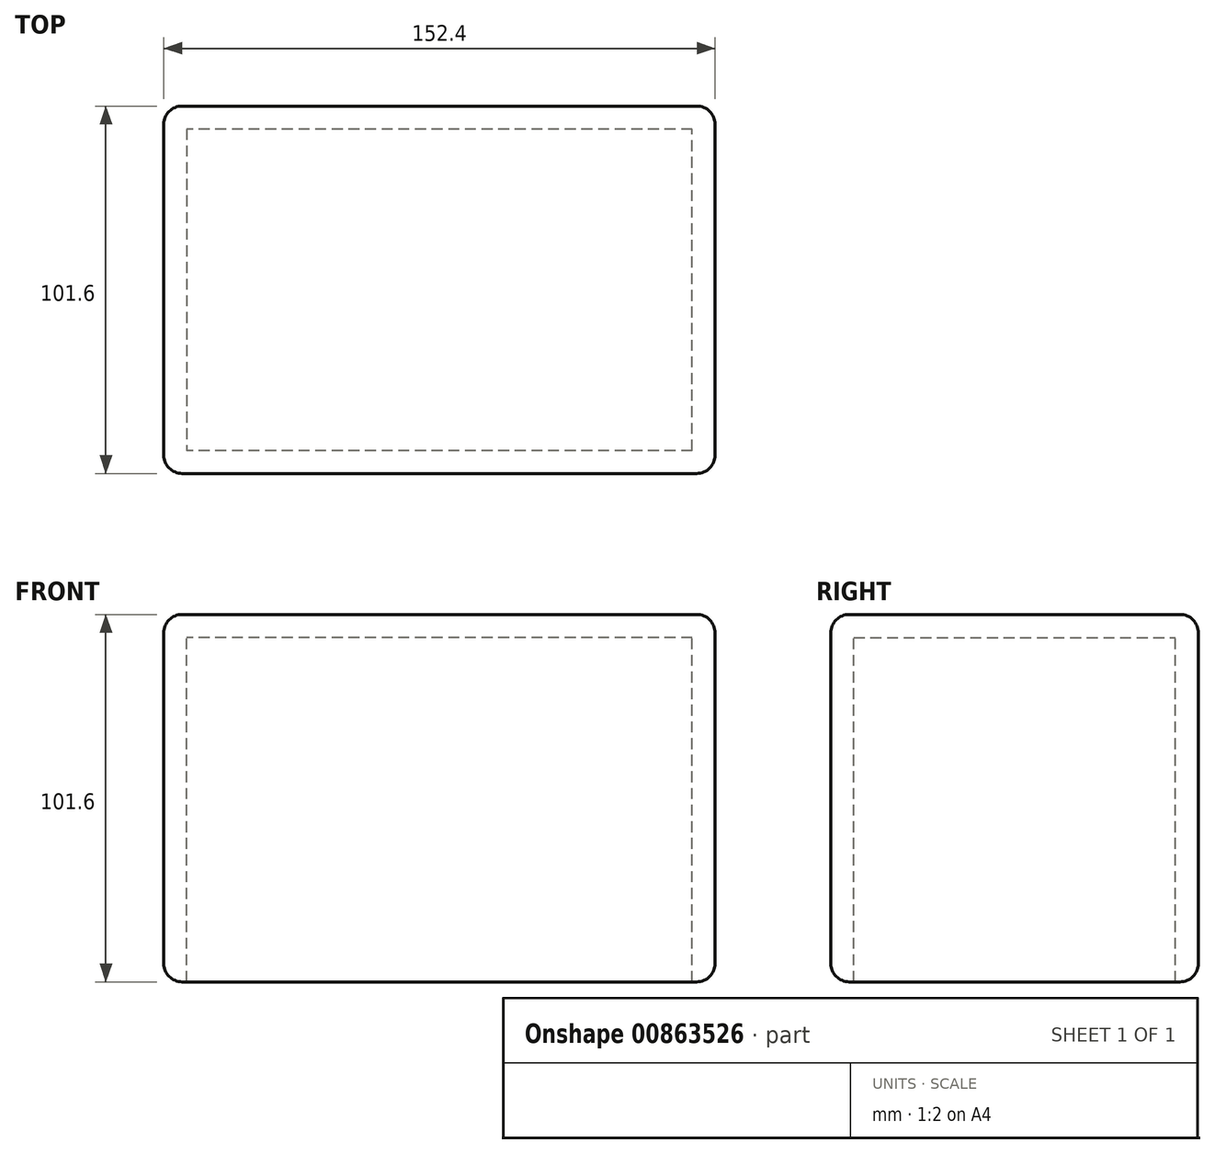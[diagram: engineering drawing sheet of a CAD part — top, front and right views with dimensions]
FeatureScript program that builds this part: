
annotation { "Feature Type Name" : "Feature", "Feature Type Description" : "" }
export const myFeature = defineFeature(function(context is Context, id is Id, definition is map)
    precondition{}
    {
        {
            var Q0;
            Q0=qCreatedBy(makeId("Top.planeOp"),FACE);
            var sketch = newSketch(context, id + "F0", { "sketchPlane" : qUnion([Q0])});
            skLineSegment(sketch, "E0.bottom", {"start": v(-111.11, 101.6) * mm, "end": v(41.29, 101.6) * mm});
            skLineSegment(sketch, "E0.top", {"start": v(-111.11, 0) * mm, "end": v(41.29, 0) * mm});
            skLineSegment(sketch, "E0.left", {"start": v(-111.11, 101.6) * mm, "end": v(-111.11, 0) * mm});
            skLineSegment(sketch, "E0.right", {"start": v(41.29, 101.6) * mm, "end": v(41.29, 0) * mm});
            skSolve(sketch);
        }
        {
            var Q0;
            Q0=makeQuery(id+"F0.imprint","IMPRINT",FACE,{"disambiguationData":[TD([[makeQuery(id+"F0.imprint","IMPRINT",EDGE,{"derivedFrom":sQuery(id+"F0.wireOp",EDGE,"E0.bottom")}),-1.0]])]});
            extrude(context, id + "F1", {"entities" : qUnion([Q0]), "depth" : 101.6 * mm, "offsetDistance" : 25.4 * mm});
        }
        {
            var Q0;
            Q0=makeQuery(id+"F1.opExtrude","CAP_EDGE",EDGE,{"disambiguationData":[OSD([sQuery(id+"F0.wireOp",EDGE,"E0.bottom")])],"isStart":false});
            var Q1;
            Q1=makeQuery(id+"F1.opExtrude","CAP_EDGE",EDGE,{"disambiguationData":[OSD([sQuery(id+"F0.wireOp",EDGE,"E0.left")])],"isStart":false});
            var Q2;
            Q2=makeQuery(id+"F1.opExtrude","CAP_EDGE",EDGE,{"disambiguationData":[OSD([sQuery(id+"F0.wireOp",EDGE,"E0.top")])],"isStart":false});
            var Q3;
            Q3=makeQuery(id+"F1.opExtrude","CAP_EDGE",EDGE,{"disambiguationData":[OSD([sQuery(id+"F0.wireOp",EDGE,"E0.right")])],"isStart":false});
            var Q4;
            Q4=makeQuery(id+"F1.opExtrude","SWEPT_EDGE",EDGE,{"disambiguationData":[OSD([sQuery(id+"F0.wireOp",EDGE,"E0.top"),sQuery(id+"F0.wireOp",EDGE,"E0.right")])]});
            var Q5;
            Q5=makeQuery(id+"F1.opExtrude","SWEPT_EDGE",EDGE,{"disambiguationData":[OSD([sQuery(id+"F0.wireOp",EDGE,"E0.top"),sQuery(id+"F0.wireOp",EDGE,"E0.left")])]});
            var Q6;
            Q6=makeQuery(id+"F1.opExtrude","SWEPT_EDGE",EDGE,{"disambiguationData":[OSD([sQuery(id+"F0.wireOp",EDGE,"E0.bottom"),sQuery(id+"F0.wireOp",EDGE,"E0.left")])]});
            var Q7;
            Q7=makeQuery(id+"F1.opExtrude","SWEPT_EDGE",EDGE,{"disambiguationData":[OSD([sQuery(id+"F0.wireOp",EDGE,"E0.bottom"),sQuery(id+"F0.wireOp",EDGE,"E0.right")])]});
            var Q8;
            Q8=makeQuery(id+"F1.opExtrude","CAP_EDGE",EDGE,{"disambiguationData":[OSD([sQuery(id+"F0.wireOp",EDGE,"E0.top")])],"isStart":true});
            var Q9;
            Q9=makeQuery(id+"F1.opExtrude","CAP_EDGE",EDGE,{"disambiguationData":[OSD([sQuery(id+"F0.wireOp",EDGE,"E0.left")])],"isStart":true});
            var Q10;
            Q10=makeQuery(id+"F1.opExtrude","CAP_EDGE",EDGE,{"disambiguationData":[OSD([sQuery(id+"F0.wireOp",EDGE,"E0.bottom")])],"isStart":true});
            var Q11;
            Q11=makeQuery(id+"F1.opExtrude","CAP_EDGE",EDGE,{"disambiguationData":[OSD([sQuery(id+"F0.wireOp",EDGE,"E0.right")])],"isStart":true});
            fillet(context, id + "F2", {"entities" : qUnion([Q0, Q1, Q2, Q3, Q4, Q5, Q6, Q7, Q8, Q9, Q10, Q11]), "radius" : 5.08 * mm, "tangentPropagation" : true, "allowEdgeOverflow" : false});
        }
        {
            var Q0;
            Q0=makeQuery(id+"F1.opExtrude","CAP_FACE",FACE,{"disambiguationData":[OSD([sQuery(id+"F0.wireOp",EDGE,"E0.bottom"),sQuery(id+"F0.wireOp",EDGE,"E0.top"),sQuery(id+"F0.wireOp",EDGE,"E0.left"),sQuery(id+"F0.wireOp",EDGE,"E0.right")])],"isStart":true});
            shell(context, id + "F3", {"entities" : qUnion([Q0]), "thickness" : 6.35 * mm});
        }
    });
